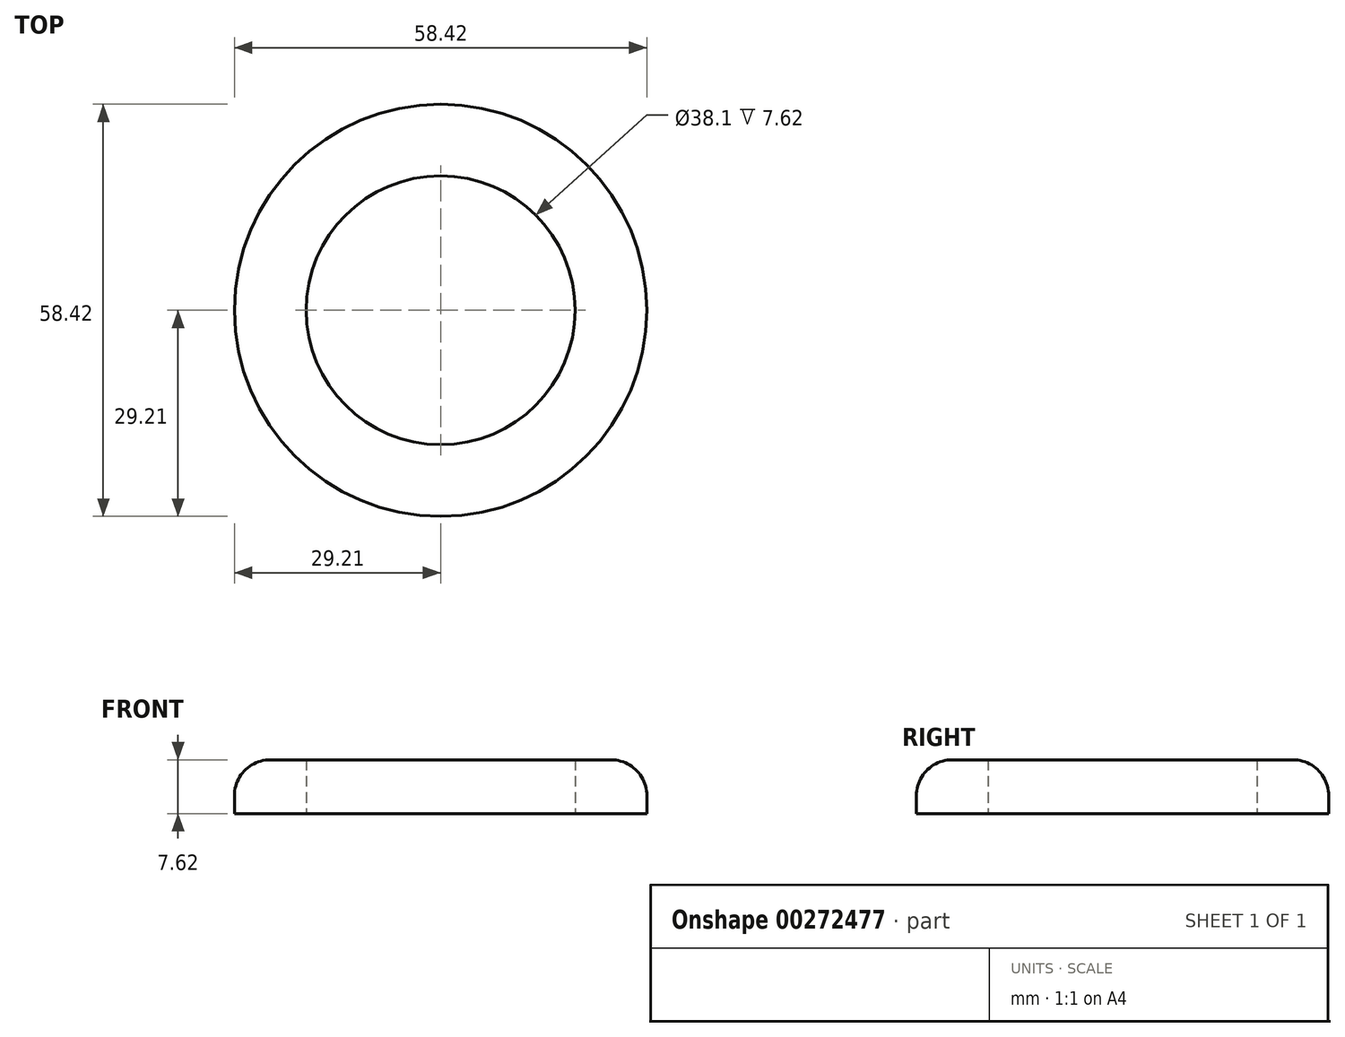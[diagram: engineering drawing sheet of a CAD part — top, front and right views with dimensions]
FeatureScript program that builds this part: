
annotation { "Feature Type Name" : "Feature", "Feature Type Description" : "" }
export const myFeature = defineFeature(function(context is Context, id is Id, definition is map)
    precondition{}
    {
        {
            var Q0;
            Q0=qCreatedBy(makeId("Top.planeOp"),FACE);
            var sketch = newSketch(context, id + "F0", { "sketchPlane" : qUnion([Q0])});
            skCircle(sketch, "E0", {"center": v(0, 0) * mm, "radius": 19.05 * mm});
            skCircle(sketch, "E1", {"center": v(0, 0) * mm, "radius": 29.21 * mm});
            skSolve(sketch);
        }
        {
            var Q0;
            Q0=qSketchRegion(id+"F0",true);
            extrude(context, id + "F1", {"entities" : qUnion([Q0]), "depth" : 7.62 * mm});
        }
        {
            var Q0;
            Q0=makeQuery(id+"F1.opExtrude","CAP_EDGE",EDGE,{"disambiguationData":[OSD([sQuery(id+"F0.wireOp",EDGE,"E1")])],"isStart":false});
            fillet(context, id + "F2", {"entities" : qUnion([Q0]), "radius" : 5.08 * mm, "tangentPropagation" : true, "allowEdgeOverflow" : false});
        }
    });
